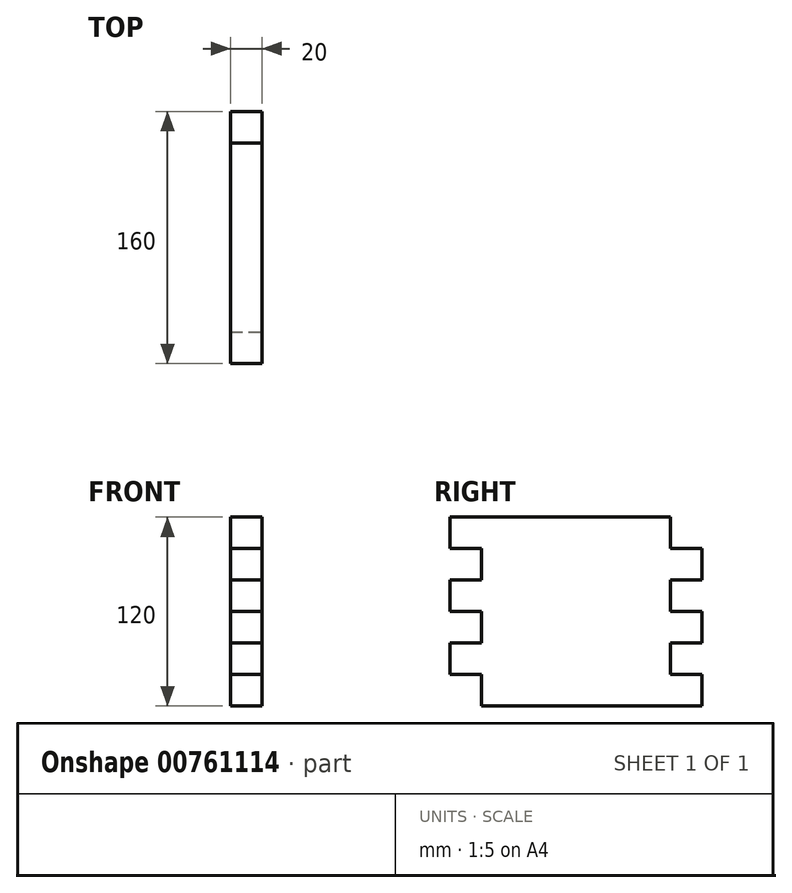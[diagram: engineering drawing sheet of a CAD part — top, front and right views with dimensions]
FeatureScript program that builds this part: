
annotation { "Feature Type Name" : "Feature", "Feature Type Description" : "" }
export const myFeature = defineFeature(function(context is Context, id is Id, definition is map)
    precondition{}
    {
        {
            var Q0;
            Q0=qCreatedBy(makeId("Right.planeOp"),FACE);
            var sketch = newSketch(context, id + "F0", { "sketchPlane" : qUnion([Q0])});
            skLineSegment(sketch, "E0.bottom", {"start": v(-244.9, 140.94) * mm, "end": v(-84.9, 140.94) * mm});
            skLineSegment(sketch, "E0.top", {"start": v(-244.9, 20.94) * mm, "end": v(-84.9, 20.94) * mm});
            skLineSegment(sketch, "E0.left", {"start": v(-244.9, 140.94) * mm, "end": v(-244.9, 20.94) * mm});
            skLineSegment(sketch, "E0.right", {"start": v(-84.9, 140.94) * mm, "end": v(-84.9, 20.94) * mm});
            skSolve(sketch);
        }
        {
            var Q0;
            Q0 = qSketchRegion(id + "F0", true);
            extrude(context, id + "F1", {"entities" : qUnion([Q0]), "depth" : 20 * mm, "offsetDistance" : 25 * mm});
        }
        {
            var Q0;
            Q0=makeQuery(id+"F1.opExtrude","CAP_FACE",FACE,{"disambiguationData":[OSD([sQuery(id+"F0.wireOp",EDGE,"E0.bottom"),sQuery(id+"F0.wireOp",EDGE,"E0.top"),sQuery(id+"F0.wireOp",EDGE,"E0.left"),sQuery(id+"F0.wireOp",EDGE,"E0.right")])],"isStart":false});
            var sketch = newSketch(context, id + "F2", { "sketchPlane" : qUnion([Q0])});
            skLineSegment(sketch, "E1.bottom", {"start": v(-244.9, 120.94) * mm, "end": v(-224.9, 120.94) * mm});
            skLineSegment(sketch, "E1.top", {"start": v(-244.9, 100.94) * mm, "end": v(-224.9, 100.94) * mm});
            skLineSegment(sketch, "E1.left", {"start": v(-244.9, 120.94) * mm, "end": v(-244.9, 100.94) * mm});
            skLineSegment(sketch, "E1.right", {"start": v(-224.9, 120.94) * mm, "end": v(-224.9, 100.94) * mm});
            skSolve(sketch);
        }
        {
            var Q0;
            Q0 = qSketchRegion(id + "F2", true);
            extrude(context, id + "F3", {"entities" : qUnion([Q0]), "operationType" : NewBodyOperationType.REMOVE, "oppositeDirection" : true, "depth" : 20 * mm, "offsetDistance" : 25 * mm});
        }
        {
            var Q0;
            Q0=makeQuery(id+"F1.opExtrude","CAP_FACE",FACE,{"disambiguationData":[OSD([sQuery(id+"F0.wireOp",EDGE,"E0.bottom"),sQuery(id+"F0.wireOp",EDGE,"E0.top"),sQuery(id+"F0.wireOp",EDGE,"E0.left"),sQuery(id+"F0.wireOp",EDGE,"E0.right")])],"isStart":false});
            var sketch = newSketch(context, id + "F4", { "sketchPlane" : qUnion([Q0])});
            skLineSegment(sketch, "E2.bottom", {"start": v(-244.9, 80.94) * mm, "end": v(-224.9, 80.94) * mm});
            skLineSegment(sketch, "E2.top", {"start": v(-244.9, 60.94) * mm, "end": v(-224.9, 60.94) * mm});
            skLineSegment(sketch, "E2.left", {"start": v(-244.9, 80.94) * mm, "end": v(-244.9, 60.94) * mm});
            skLineSegment(sketch, "E2.right", {"start": v(-224.9, 80.94) * mm, "end": v(-224.9, 60.94) * mm});
            skSolve(sketch);
        }
        {
            var Q0;
            Q0 = qSketchRegion(id + "F4", true);
            extrude(context, id + "F5", {"entities" : qUnion([Q0]), "operationType" : NewBodyOperationType.REMOVE, "oppositeDirection" : true, "depth" : 20 * mm, "offsetDistance" : 25 * mm});
        }
        {
            var Q0;
            Q0=makeQuery(id+"F1.opExtrude","CAP_FACE",FACE,{"disambiguationData":[OSD([sQuery(id+"F0.wireOp",EDGE,"E0.bottom"),sQuery(id+"F0.wireOp",EDGE,"E0.top"),sQuery(id+"F0.wireOp",EDGE,"E0.left"),sQuery(id+"F0.wireOp",EDGE,"E0.right")])],"isStart":false});
            var sketch = newSketch(context, id + "F6", { "sketchPlane" : qUnion([Q0])});
            skLineSegment(sketch, "E3.bottom", {"start": v(-244.9, 20.94) * mm, "end": v(-224.9, 20.94) * mm});
            skLineSegment(sketch, "E3.top", {"start": v(-244.9, 40.94) * mm, "end": v(-224.9, 40.94) * mm});
            skLineSegment(sketch, "E3.left", {"start": v(-244.9, 20.94) * mm, "end": v(-244.9, 40.94) * mm});
            skLineSegment(sketch, "E3.right", {"start": v(-224.9, 20.94) * mm, "end": v(-224.9, 40.94) * mm});
            skSolve(sketch);
        }
        {
            var Q0;
            Q0 = qSketchRegion(id + "F6", true);
            extrude(context, id + "F7", {"entities" : qUnion([Q0]), "operationType" : NewBodyOperationType.REMOVE, "oppositeDirection" : true, "depth" : 20 * mm, "offsetDistance" : 25 * mm});
        }
        {
            var Q0;
            Q0=makeQuery(id+"F1.opExtrude","CAP_FACE",FACE,{"disambiguationData":[OSD([sQuery(id+"F0.wireOp",EDGE,"E0.bottom"),sQuery(id+"F0.wireOp",EDGE,"E0.top"),sQuery(id+"F0.wireOp",EDGE,"E0.left"),sQuery(id+"F0.wireOp",EDGE,"E0.right")])],"isStart":false});
            var sketch = newSketch(context, id + "F8", { "sketchPlane" : qUnion([Q0])});
            skLineSegment(sketch, "E4.bottom", {"start": v(-84.9, 140.94) * mm, "end": v(-104.9, 140.94) * mm});
            skLineSegment(sketch, "E4.top", {"start": v(-84.9, 120.94) * mm, "end": v(-104.9, 120.94) * mm});
            skLineSegment(sketch, "E4.left", {"start": v(-84.9, 140.94) * mm, "end": v(-84.9, 120.94) * mm});
            skLineSegment(sketch, "E4.right", {"start": v(-104.9, 140.94) * mm, "end": v(-104.9, 120.94) * mm});
            skSolve(sketch);
        }
        {
            var Q0;
            Q0 = qSketchRegion(id + "F8", true);
            extrude(context, id + "F9", {"entities" : qUnion([Q0]), "operationType" : NewBodyOperationType.REMOVE, "oppositeDirection" : true, "depth" : 20 * mm, "offsetDistance" : 25 * mm});
        }
        {
            var Q0;
            Q0=makeQuery(id+"F1.opExtrude","CAP_FACE",FACE,{"disambiguationData":[OSD([sQuery(id+"F0.wireOp",EDGE,"E0.bottom"),sQuery(id+"F0.wireOp",EDGE,"E0.top"),sQuery(id+"F0.wireOp",EDGE,"E0.left"),sQuery(id+"F0.wireOp",EDGE,"E0.right")])],"isStart":false});
            var sketch = newSketch(context, id + "F10", { "sketchPlane" : qUnion([Q0])});
            skLineSegment(sketch, "E5.bottom", {"start": v(-84.9, 100.94) * mm, "end": v(-104.9, 100.94) * mm});
            skLineSegment(sketch, "E5.top", {"start": v(-84.9, 80.94) * mm, "end": v(-104.9, 80.94) * mm});
            skLineSegment(sketch, "E5.left", {"start": v(-84.9, 100.94) * mm, "end": v(-84.9, 80.94) * mm});
            skLineSegment(sketch, "E5.right", {"start": v(-104.9, 100.94) * mm, "end": v(-104.9, 80.94) * mm});
            skSolve(sketch);
        }
        {
            var Q0;
            Q0 = qSketchRegion(id + "F10", true);
            extrude(context, id + "F11", {"entities" : qUnion([Q0]), "operationType" : NewBodyOperationType.REMOVE, "oppositeDirection" : true, "depth" : 20 * mm, "offsetDistance" : 25 * mm});
        }
        {
            var Q0;
            Q0=makeQuery(id+"F1.opExtrude","CAP_FACE",FACE,{"disambiguationData":[OSD([sQuery(id+"F0.wireOp",EDGE,"E0.bottom"),sQuery(id+"F0.wireOp",EDGE,"E0.top"),sQuery(id+"F0.wireOp",EDGE,"E0.left"),sQuery(id+"F0.wireOp",EDGE,"E0.right")])],"isStart":false});
            var sketch = newSketch(context, id + "F12", { "sketchPlane" : qUnion([Q0])});
            skLineSegment(sketch, "E6.bottom", {"start": v(-84.9, 60.94) * mm, "end": v(-104.9, 60.94) * mm});
            skLineSegment(sketch, "E6.top", {"start": v(-84.9, 40.94) * mm, "end": v(-104.9, 40.94) * mm});
            skLineSegment(sketch, "E6.left", {"start": v(-84.9, 60.94) * mm, "end": v(-84.9, 40.94) * mm});
            skLineSegment(sketch, "E6.right", {"start": v(-104.9, 60.94) * mm, "end": v(-104.9, 40.94) * mm});
            skSolve(sketch);
        }
        {
            var Q0;
            Q0 = qSketchRegion(id + "F12", true);
            extrude(context, id + "F13", {"entities" : qUnion([Q0]), "operationType" : NewBodyOperationType.REMOVE, "oppositeDirection" : true, "depth" : 20 * mm, "offsetDistance" : 25 * mm});
        }
    });
